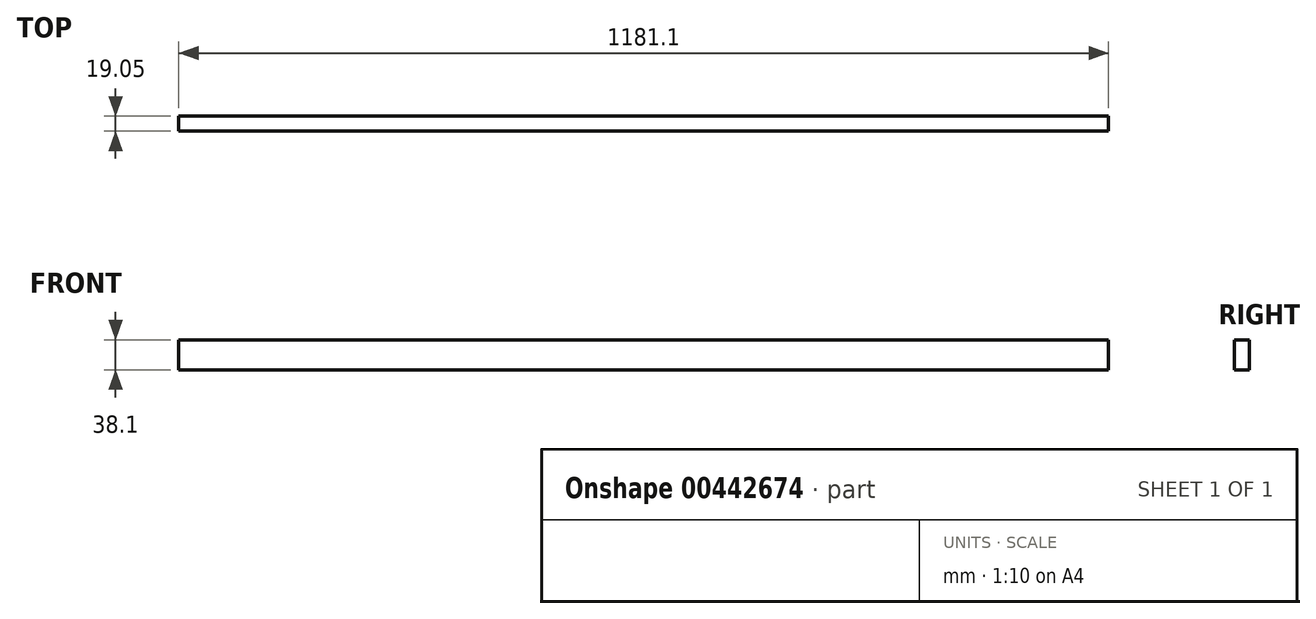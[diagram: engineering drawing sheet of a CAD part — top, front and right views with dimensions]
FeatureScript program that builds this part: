
annotation { "Feature Type Name" : "Feature", "Feature Type Description" : "" }
export const myFeature = defineFeature(function(context is Context, id is Id, definition is map)
    precondition{}
    {
        {
            var Q0;
            Q0=qCreatedBy(makeId("Front.planeOp"),FACE);
            var sketch = newSketch(context, id + "F0", { "sketchPlane" : qUnion([Q0])});
            skLineSegment(sketch, "E0.bottom", {"start": v(0, 0) * mm, "end": v(1181.1, 0) * mm});
            skLineSegment(sketch, "E0.top", {"start": v(0, 38.1) * mm, "end": v(1181.1, 38.1) * mm});
            skLineSegment(sketch, "E0.left", {"start": v(0, 0) * mm, "end": v(0, 38.1) * mm});
            skLineSegment(sketch, "E0.right", {"start": v(1181.1, 0) * mm, "end": v(1181.1, 38.1) * mm});
            skSolve(sketch);
        }
        {
            var Q0;
            Q0 = qSketchRegion(id + "F0", true);
            extrude(context, id + "F1", {"entities" : qUnion([Q0]), "depth" : 19.05 * mm});
        }
    });
